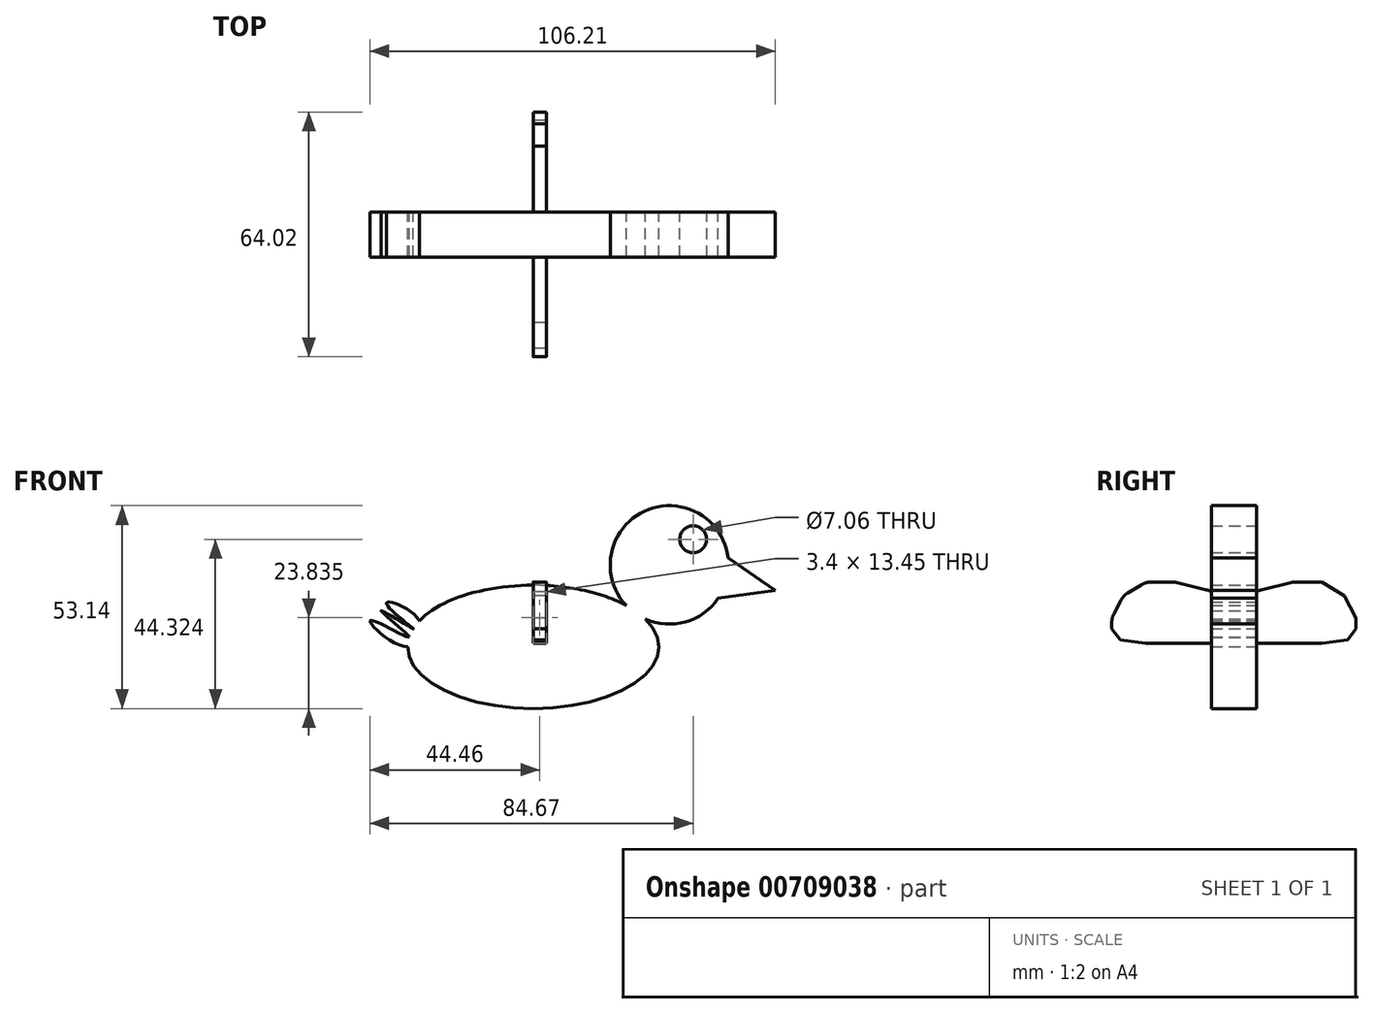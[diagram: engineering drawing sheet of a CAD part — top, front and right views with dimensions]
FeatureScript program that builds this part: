
annotation { "Feature Type Name" : "Feature", "Feature Type Description" : "" }
export const myFeature = defineFeature(function(context is Context, id is Id, definition is map)
    precondition{}
    {
        {
            var Q0;
            Q0=qCreatedBy(makeId("Front.planeOp"),FACE);
            var sketch = newSketch(context, id + "F0", { "sketchPlane" : qUnion([Q0])});
            skCircle(sketch, "E0", {"center": v(35.68, 12) * mm, "radius": 15.51 * mm});
            skEllipse(sketch, "E1", {"center": v(0, -9.47) * mm, "majorRadius": 32.9 * mm, "minorRadius": 16.15 * mm, "majorAxis": v(-1, 0)});
            skLineSegment(sketch, "E2", {"start": v(51.08, 13.8) * mm, "end": v(63.45, 5.33) * mm});
            skLineSegment(sketch, "E3", {"start": v(63.45, 5.33) * mm, "end": v(48.47, 3.24) * mm});
            skFitSpline(sketch, "E4", {"points": [v(-29.8, -2.63) * mm, v(-38.45, 1.85) * mm, v(-31.46, -4.73) * mm, v(-39.83, 0) * mm, v(-32.5, -6.91) * mm, v(-42.6, -2.54) * mm, v(-32.9, -9.47) * mm, v(-29.8, -2.63) * mm]});
            skCircle(sketch, "E5", {"center": v(41.91, 18.7) * mm, "radius": 3.53 * mm});
            skLineSegment(sketch, "E6", {"start": v(50.72, 8.24) * mm, "end": v(62.53, 5.2) * mm});
            skLineSegment(sketch, "E7", {"start": v(50.72, 8.24) * mm, "end": v(62.48, 5.99) * mm});
            skSolve(sketch);
        }
        {
            var Q0;
            Q0=qCreatedBy(makeId("Right.planeOp"),FACE);
            var sketch = newSketch(context, id + "F1", { "sketchPlane" : qUnion([Q0])});
            skLineSegment(sketch, "E8", {"start": v(0, 0) * mm, "end": v(5.19, 4.43) * mm});
            skLineSegment(sketch, "E9", {"start": v(7.26, 5.49) * mm, "end": v(14.91, 7.35) * mm});
            skLineSegment(sketch, "E10", {"start": v(16.1, 7.5) * mm, "end": v(23.12, 7.5) * mm});
            skLineSegment(sketch, "E11", {"start": v(23.12, 7.5) * mm, "end": v(28.96, 3.94) * mm});
            skLineSegment(sketch, "E12", {"start": v(28.96, 3.94) * mm, "end": v(32, -1.9) * mm});
            skLineSegment(sketch, "E13", {"start": v(32, -1.9) * mm, "end": v(32, -4.7) * mm});
            skLineSegment(sketch, "E14", {"start": v(23.12, -8.51) * mm, "end": v(15.75, -8.51) * mm});
            skLineSegment(sketch, "E15", {"start": v(15.75, -8.51) * mm, "end": v(8.9, -8.51) * mm});
            skLineSegment(sketch, "E16", {"start": v(8.9, -8.51) * mm, "end": v(3.3, -8.51) * mm});
            skLineSegment(sketch, "E17", {"start": v(3.3, -8.51) * mm, "end": v(0, -8.51) * mm});
            skLineSegment(sketch, "E18", {"start": v(32, -4.7) * mm, "end": v(29.8, -7.59) * mm});
            skLineSegment(sketch, "E19", {"start": v(29.8, -7.59) * mm, "end": v(23.12, -8.51) * mm});
            skPoint(sketch, "E20.visualSharp", {"position": v(15.5, 7.5) * mm});
            skArc(sketch, "E20.filletArc", {"start": v(16.1, 7.5) * mm, "mid": v(15.5, 7.46) * mm, "end": v(14.91, 7.35) * mm});
            skPoint(sketch, "E21.visualSharp", {"position": v(6.1, 5.2) * mm});
            skArc(sketch, "E21.filletArc", {"start": v(7.26, 5.49) * mm, "mid": v(6.16, 5.08) * mm, "end": v(5.19, 4.43) * mm});
            skArc(sketch, "E22.MirrorCS", {"start": v(-16.1, 7.5) * mm, "mid": v(-15.5, 7.46) * mm, "end": v(-14.91, 7.35) * mm});
            skLineSegment(sketch, "E23.MirrorCS", {"start": v(-32, -1.9) * mm, "end": v(-32, -4.7) * mm});
            skArc(sketch, "E24.MirrorCS", {"start": v(-7.26, 5.49) * mm, "mid": v(-6.16, 5.08) * mm, "end": v(-5.19, 4.43) * mm});
            skLineSegment(sketch, "E25.MirrorCS", {"start": v(-16.1, 7.5) * mm, "end": v(-23.12, 7.5) * mm});
            skLineSegment(sketch, "E26.MirrorCS", {"start": v(-32, -4.7) * mm, "end": v(-29.8, -7.59) * mm});
            skLineSegment(sketch, "E27.MirrorCS", {"start": v(-3.3, -8.51) * mm, "end": v(0, -8.51) * mm});
            skLineSegment(sketch, "E28.MirrorCS", {"start": v(-15.75, -8.51) * mm, "end": v(-8.9, -8.51) * mm});
            skLineSegment(sketch, "E29.MirrorCS", {"start": v(-23.12, -8.51) * mm, "end": v(-15.75, -8.51) * mm});
            skLineSegment(sketch, "E30.MirrorCS", {"start": v(-8.9, -8.51) * mm, "end": v(-3.3, -8.51) * mm});
            skLineSegment(sketch, "E31.MirrorCS", {"start": v(-29.8, -7.59) * mm, "end": v(-23.12, -8.51) * mm});
            skPoint(sketch, "E32.MirrorP", {"position": v(-6.1, 5.2) * mm});
            skPoint(sketch, "E33.MirrorP", {"position": v(-15.5, 7.5) * mm});
            skLineSegment(sketch, "E34.MirrorCS", {"start": v(-7.26, 5.49) * mm, "end": v(-14.91, 7.35) * mm});
            skLineSegment(sketch, "E35.MirrorCS", {"start": v(-23.12, 7.5) * mm, "end": v(-28.96, 3.94) * mm});
            skLineSegment(sketch, "E36.MirrorCS", {"start": v(0, 0) * mm, "end": v(-5.19, 4.43) * mm});
            skLineSegment(sketch, "E37.MirrorCS", {"start": v(-28.96, 3.94) * mm, "end": v(-32, -1.9) * mm});
            skSolve(sketch);
        }
        {
            var Q0;
            Q0 = qSketchRegion(id + "F1", true);
            extrude(context, id + "F2", {"entities" : qUnion([Q0]), "depth" : 3.4 * mm, "offsetDistance" : 25 * mm});
        }
        {
            var Q0;
            Q0 = qSketchRegion(id + "F0", true);
            extrude(context, id + "F3", {"entities" : qUnion([Q0]), "operationType" : NewBodyOperationType.ADD, "depth" : 5.9 * mm, "offsetDistance" : 25 * mm});
        }
        {
            var Q0;
            Q0=makeQuery(id+"F2.opExtrude","SWEPT_BODY",BODY,{"disambiguationData":[OSD([sQuery(id+"F1.wireOp",EDGE,"E8"),sQuery(id+"F1.wireOp",EDGE,"E9"),sQuery(id+"F1.wireOp",EDGE,"E10"),sQuery(id+"F1.wireOp",EDGE,"E11"),sQuery(id+"F1.wireOp",EDGE,"E12"),sQuery(id+"F1.wireOp",EDGE,"E13"),sQuery(id+"F1.wireOp",EDGE,"E14"),sQuery(id+"F1.wireOp",EDGE,"E15"),sQuery(id+"F1.wireOp",EDGE,"E16"),sQuery(id+"F1.wireOp",EDGE,"E17"),sQuery(id+"F1.wireOp",EDGE,"E18"),sQuery(id+"F1.wireOp",EDGE,"E19"),sQuery(id+"F1.wireOp",EDGE,"E20.filletArc"),sQuery(id+"F1.wireOp",EDGE,"E21.filletArc"),sQuery(id+"F1.wireOp",EDGE,"E22.MirrorCS"),sQuery(id+"F1.wireOp",EDGE,"E23.MirrorCS"),sQuery(id+"F1.wireOp",EDGE,"E24.MirrorCS"),sQuery(id+"F1.wireOp",EDGE,"E25.MirrorCS"),sQuery(id+"F1.wireOp",EDGE,"E26.MirrorCS"),sQuery(id+"F1.wireOp",EDGE,"E27.MirrorCS"),sQuery(id+"F1.wireOp",EDGE,"E28.MirrorCS"),sQuery(id+"F1.wireOp",EDGE,"E29.MirrorCS"),sQuery(id+"F1.wireOp",EDGE,"E30.MirrorCS"),sQuery(id+"F1.wireOp",EDGE,"E31.MirrorCS"),sQuery(id+"F1.wireOp",EDGE,"E34.MirrorCS"),sQuery(id+"F1.wireOp",EDGE,"E35.MirrorCS"),sQuery(id+"F1.wireOp",EDGE,"E36.MirrorCS"),sQuery(id+"F1.wireOp",EDGE,"E37.MirrorCS")])]});
            var Q1;
            Q1=qCreatedBy(makeId("Front.planeOp"),FACE);
            mirror(context, id + "F4", {"operationType" : NewBodyOperationType.ADD, "entities" : qUnion([Q0]), "mirrorPlane" : qUnion([Q1])});
        }
        {
            var Q0;
            Q0=makeQuery(id+"F2.opExtrude","SWEPT_EDGE",EDGE,{"disambiguationData":[OSD([sQuery(id+"F1.wireOp",EDGE,"E35.MirrorCS"),sQuery(id+"F1.wireOp",EDGE,"E37.MirrorCS")])]});
            var Q1;
            Q1=makeQuery(id+"F2.opExtrude","SWEPT_EDGE",EDGE,{"disambiguationData":[OSD([sQuery(id+"F1.wireOp",EDGE,"E25.MirrorCS"),sQuery(id+"F1.wireOp",EDGE,"E35.MirrorCS")])]});
            var Q2;
            Q2=makeQuery(id+"F2.opExtrude","SWEPT_EDGE",EDGE,{"disambiguationData":[OSD([sQuery(id+"F1.wireOp",EDGE,"E22.MirrorCS"),sQuery(id+"F1.wireOp",EDGE,"E25.MirrorCS")])]});
            var Q3;
            Q3=makeQuery(id+"F2.opExtrude","SWEPT_EDGE",EDGE,{"disambiguationData":[OSD([sQuery(id+"F1.wireOp",EDGE,"E23.MirrorCS"),sQuery(id+"F1.wireOp",EDGE,"E37.MirrorCS")])]});
            fillet(context, id + "F5", {"entities" : qUnion([Q0, Q1, Q2, Q3]), "tangentPropagation" : true, "radius" : 5 * mm, "defaultsChanged" : false, "vertexSettings" : [], "allowEdgeOverflow" : false});
        }
    });
